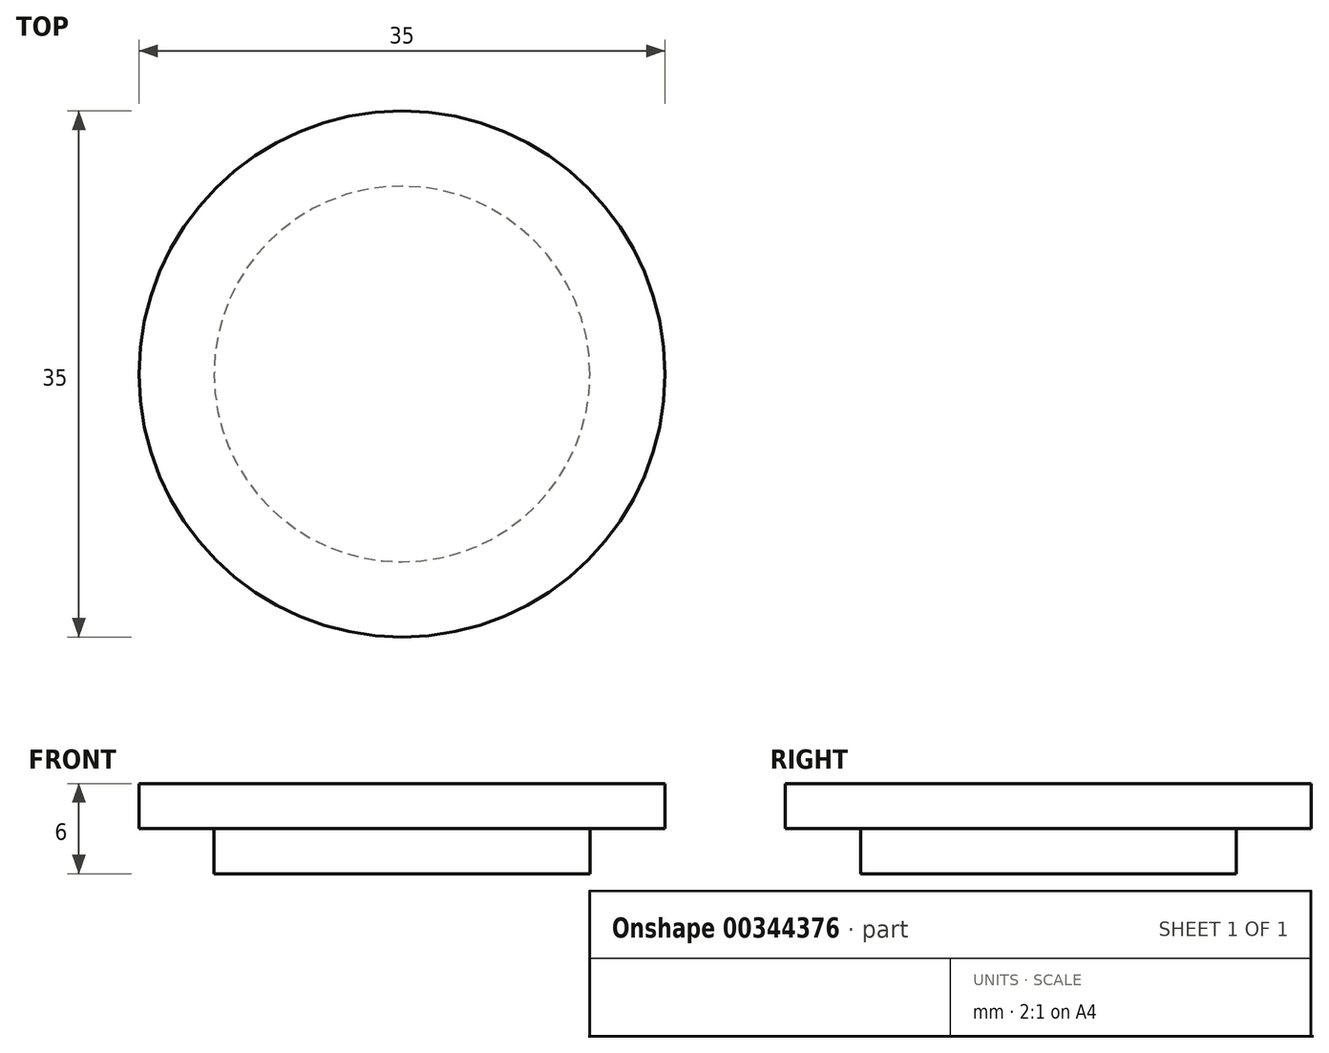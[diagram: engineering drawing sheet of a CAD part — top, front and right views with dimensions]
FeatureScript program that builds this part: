
annotation { "Feature Type Name" : "Feature", "Feature Type Description" : "" }
export const myFeature = defineFeature(function(context is Context, id is Id, definition is map)
    precondition{}
    {
        {
            var Q0;
            Q0=qCreatedBy(makeId("Top.planeOp"),FACE);
            var sketch = newSketch(context, id + "F0", { "sketchPlane" : qUnion([Q0])});
            skCircle(sketch, "E0", {"center": v(0, 0) * mm, "radius": 17.5 * mm});
            skSolve(sketch);
        }
        {
            var Q0;
            Q0=makeQuery(id+"F0.imprint","IMPRINT",FACE,{"disambiguationData":[TD([[makeQuery(id+"F0.imprint","IMPRINT",EDGE,{"derivedFrom":sQuery(id+"F0.wireOp",EDGE,"E0")}),1.0]])]});
            extrude(context, id + "F1", {"entities" : qUnion([Q0]), "depth" : 3 * mm});
        }
        {
            var Q0;
            Q0=qCreatedBy(makeId("Top.planeOp"),FACE);
            var sketch = newSketch(context, id + "F2", { "sketchPlane" : qUnion([Q0])});
            skCircle(sketch, "E1", {"center": v(0, 0) * mm, "radius": 12.5 * mm});
            skSolve(sketch);
        }
        {
            var Q0;
            Q0 = qSketchRegion(id + "F2", true);
            extrude(context, id + "F3", {"entities" : qUnion([Q0]), "operationType" : NewBodyOperationType.ADD, "oppositeDirection" : true, "depth" : 3 * mm});
        }
    });
